# Revit family: axor_basic_set_40_l_min_for_shut_off_valve_16974180
name_source: partatom
category: Plumbing Fixtures
revit_build: Autodesk Revit 2015 (Build: 20140903_1530(x64)
units: mm (PartAtom-declared; Revit-internal decimal feet)

## types (1)
- n.a.
    BIMobject category = Valves
    BOSUseNativeGeometries = 1
    Default Elevation = 4' - 0"
    Design country = Germany
    EAN code = https://4059625032398
    Edition number = 1
    IFC Classification = Sanitary Terminal
    Installation instructions = https://pro.hansgrohe-int.com
    Manufacturer country = Germany
    Manufacturer name = AXOR
    Masterformat 2014 Code = 33 12 16
    Masterformat 2014 Description = Water Utility Distribution Valves
    NBS Reference Code = 94-93
    NBS Reference Description = Valve Accessories
    Nominal height = 0
    Nominal width = 0
    OmniClass Code = 23-27 31 00
    OmniClass Description = Valves
    Product Guid = 1535d8eb-7446-45bc-a2e3-160383949210
    Product SKU = 16974180
    Product data url = https://bimobject.com
    Product family = AXOR Basic sets
    Product group = Shut-off valves
    Product name = AXOR Basic set 40 l/min for shut-off valve 16974180
    Product url = https://pro.hansgrohe-int.com
    QR code = http://bimobject.com
    Technical description = https://pro.hansgrohe-int.com
    UNSPSC Code = 401416
    Uniclass 1.4 Code = L7117
    Uniclass 1.4 Description = Valves for water supply/distribution
    Uniclass 2.0 Code = PR-94-93
    Uniclass 2.0 Description = Valve Accessories
    Uniclass 2015 Code = Pr_40_20_87_80
    Uniclass 2015 Name = Shower thermostatic valves
    Uniformat II Code = D2010
    Uniformat II Description = Plumbing Fixtures
    Weight Net (Kg) = 0

## geometry (parser evidence)
native form markers: Sweep x2
no freeform markers — native parametric forms only
